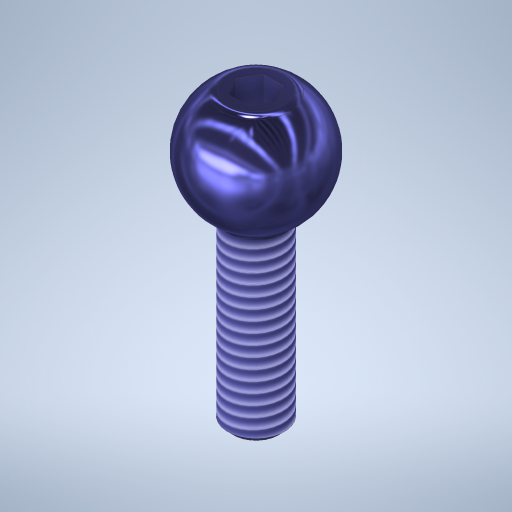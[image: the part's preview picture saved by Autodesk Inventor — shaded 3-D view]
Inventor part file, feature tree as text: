
AUTODESK INVENTOR PART (.ipt)
format: ipt  version: 2023.1 (Build 271208000, 208)  size: 388,608 bytes
history: native  units: in
note: dims shown in document units (in); Inventor stores cm internally (conversion verified against a paired STEP export)
features: sketch x3, fillet x2, revolve x1, chamfer x1, plane x1, split x1, extrude x1, thread x1, projected_geometry x1
ambient origin geometry x8: Origin, YZ Plane, XZ Plane, XY Plane, X Axis, Y Axis, Z Axis, Center Point
bodies: Solid1 (feature_tree)
feature tree (12):
  revolve  "Revolution1"  [1 undecoded]
  fillet  "Fillet1"  Radius=0.15in
  chamfer  "Chamfer1"  Distance=0.015in Angle=45.0deg
  sketch  "Sketch2"  dims[d3=90.0deg]
  plane  "Work Plane2"
  split  "Split1"
  fillet  "Fillet2"  Radius=0.1625in
  extrude  "Extrusion1"  Depth=0.032in
  thread  "Thread1"  [1 undecoded]
  sketch  "Sketch1"  dims[d0=0.325in d1=0.625in d2=0.15in]
  sketch  "Sketch3"  dims[d4=0.015in d5=0.015in d6=0.125in d7=45.0deg d8=0.1625in d9=0.032in d10=0.0938in d11=0.1in d12=0.0in d13=1.0in d14=0.0in]
  projected_geometry  "Project Cut Edges1"
note: 2 required parameter values undecoded (feature->parameter linkage not recoverable at this tier; creation-order binding heuristic only, values carry confidence <= 0.55)